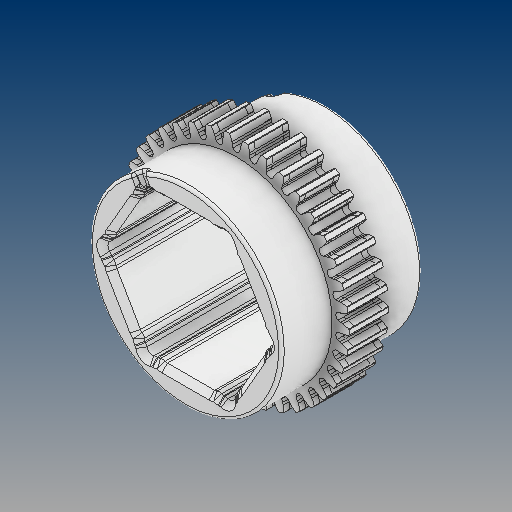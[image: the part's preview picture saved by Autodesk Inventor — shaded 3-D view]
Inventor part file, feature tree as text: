
AUTODESK INVENTOR PART (.ipt)
format: ipt  version: 2024.3 (Build 283343000, 343)  size: 2,167,296 bytes
history: native  units: in
note: dims shown in document units (in); Inventor stores cm internally (conversion verified against a paired STEP export)
features: fillet x1
ambient origin geometry x8: Origin, YZ Plane, XZ Plane, XY Plane, X Axis, Y Axis, Z Axis, Center Point
bodies: Solid1 (feature_tree)
feature tree (1):
  fillet  "Fillet5"  [1 undecoded]
note: 1 required parameter value undecoded (feature->parameter linkage not recoverable at this tier; creation-order binding heuristic only, values carry confidence <= 0.55)
